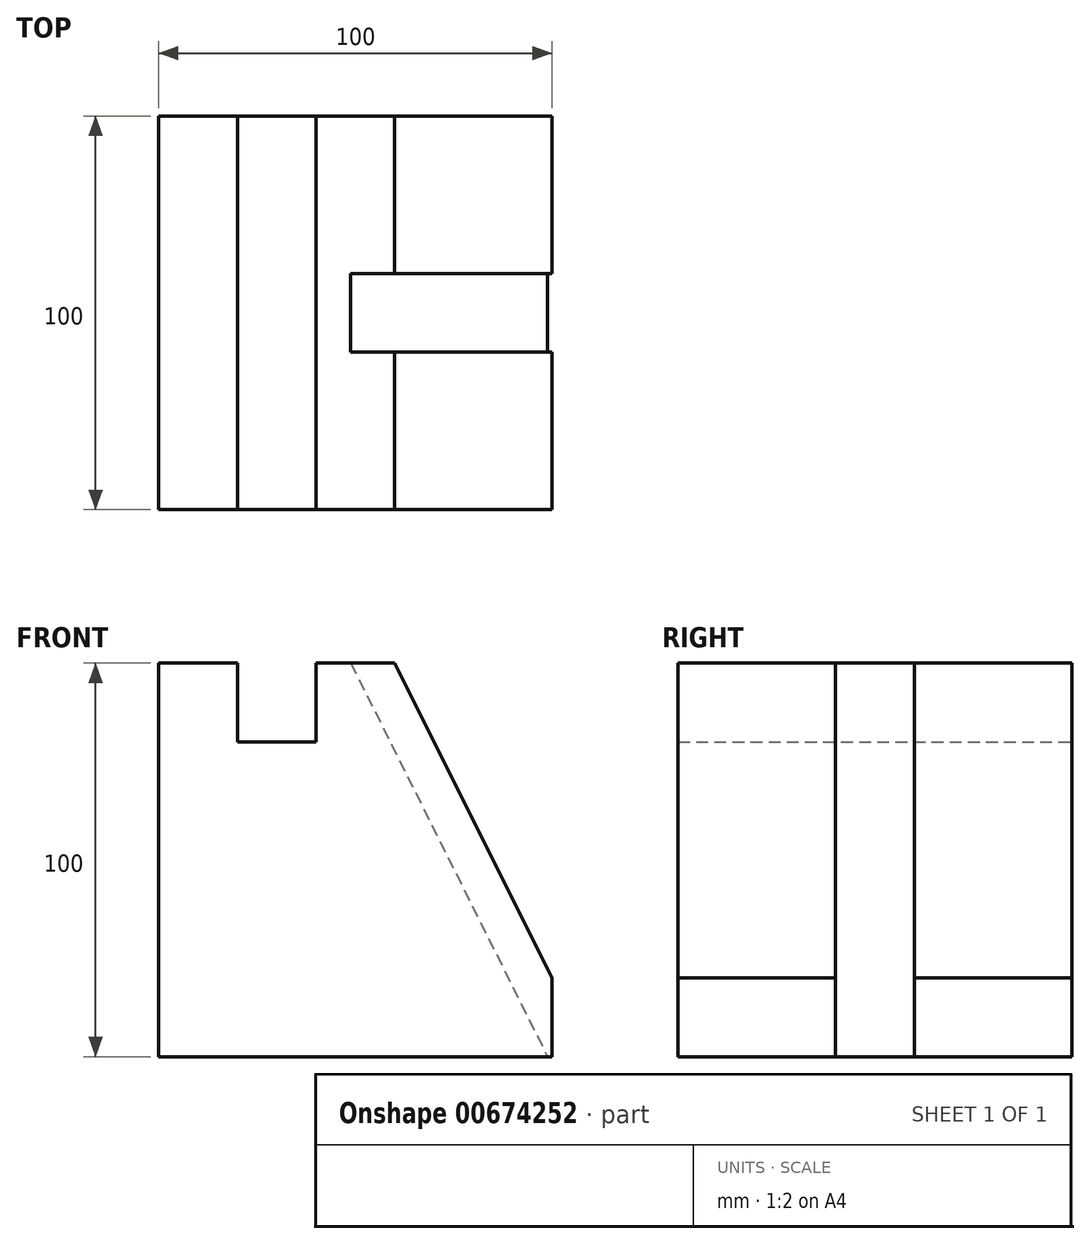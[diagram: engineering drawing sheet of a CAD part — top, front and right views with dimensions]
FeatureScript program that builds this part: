
annotation { "Feature Type Name" : "Feature", "Feature Type Description" : "" }
export const myFeature = defineFeature(function(context is Context, id is Id, definition is map)
    precondition{}
    {
        {
            var Q0;
            Q0=qCreatedBy(makeId("Front.planeOp"),FACE);
            var sketch = newSketch(context, id + "F0", { "sketchPlane" : qUnion([Q0])});
            skLineSegment(sketch, "E0", {"start": v(0, 0) * mm, "end": v(0, 100) * mm});
            skLineSegment(sketch, "E1", {"start": v(0, 0) * mm, "end": v(100, 0) * mm});
            skLineSegment(sketch, "E2", {"start": v(100, 0) * mm, "end": v(100, 20) * mm});
            skLineSegment(sketch, "E3", {"start": v(0, 100) * mm, "end": v(20, 100) * mm});
            skLineSegment(sketch, "E4", {"start": v(20, 100) * mm, "end": v(20, 80) * mm});
            skLineSegment(sketch, "E5", {"start": v(20, 80) * mm, "end": v(40, 80) * mm});
            skLineSegment(sketch, "E6", {"start": v(40, 80) * mm, "end": v(40, 100) * mm});
            skLineSegment(sketch, "E7", {"start": v(40, 100) * mm, "end": v(60, 100) * mm});
            skLineSegment(sketch, "E8", {"start": v(60, 100) * mm, "end": v(100, 20) * mm});
            skSolve(sketch);
        }
        {
            var Q0;
            Q0=makeQuery(id+"F0.imprint","IMPRINT",FACE,{"disambiguationData":[TD([[makeQuery(id+"F0.imprint","IMPRINT",EDGE,{"derivedFrom":sQuery(id+"F0.wireOp",EDGE,"E0")}),-1.0]])]});
            extrude(context, id + "F1", {"entities" : qUnion([Q0]), "depth" : 100 * mm, "offsetDistance" : 25 * mm});
        }
        {
            var Q0;
            Q0=makeQuery(id+"F1.opExtrude","SWEPT_FACE",FACE,{"disambiguationData":[OSD([sQuery(id+"F0.wireOp",EDGE,"E8")])]});
            var sketch = newSketch(context, id + "F2", { "sketchPlane" : qUnion([Q0])});
            skLineSegment(sketch, "E9", {"start": v(-100, 62.6) * mm, "end": v(-60, 62.6) * mm});
            skLineSegment(sketch, "E10", {"start": v(-60, 62.6) * mm, "end": v(-40, 62.6) * mm});
            skLineSegment(sketch, "E11", {"start": v(-40, 62.6) * mm, "end": v(0, 62.6) * mm});
            skLineSegment(sketch, "E12", {"start": v(-60, 62.6) * mm, "end": v(-60, -26.83) * mm});
            skLineSegment(sketch, "E13", {"start": v(-60, -26.83) * mm, "end": v(-40, -26.83) * mm});
            skLineSegment(sketch, "E14", {"start": v(-40, -26.83) * mm, "end": v(-40, 62.6) * mm});
            skSolve(sketch);
        }
        {
            var Q0;
            Q0=makeQuery(id+"F2.imprint","IMPRINT",FACE,{"disambiguationData":[TD([[makeQuery(id+"F2.imprint","IMPRINT",EDGE,{"derivedFrom":sQuery(id+"F2.wireOp",EDGE,"E12")}),1.0]])]});
            extrude(context, id + "F3", {"entities" : qUnion([Q0]), "operationType" : NewBodyOperationType.REMOVE, "oppositeDirection" : true, "depth" : 10 * mm, "offsetDistance" : 25 * mm});
        }
        {
            var Q0;
            Q0=makeQuery(id+"F3.boolean.opBoolean","COPY",FACE,{"derivedFrom":makeQuery(id+"F3.opExtrude","SWEPT_FACE",FACE,{"disambiguationData":[OSD([sQuery(id+"F2.wireOp",EDGE,"E10")])]})});
            extrude(context, id + "F4", {"entities" : qUnion([Q0]), "operationType" : NewBodyOperationType.REMOVE, "oppositeDirection" : true, "depth" : 10 * mm, "offsetDistance" : 25 * mm});
        }
        {
            var Q0;
            Q0=makeQuery(id+"F3.boolean.opBoolean","COPY",FACE,{"derivedFrom":makeQuery(id+"F3.opExtrude","SWEPT_FACE",FACE,{"disambiguationData":[OSD([sQuery(id+"F2.wireOp",EDGE,"E13")])]})});
            extrude(context, id + "F5", {"entities" : qUnion([Q0]), "operationType" : NewBodyOperationType.REMOVE, "oppositeDirection" : true, "depth" : 10 * mm, "offsetDistance" : 25 * mm});
        }
        {
            var Q0;
            Q0=makeQuery(id+"F5.boolean.opBoolean","COPY",FACE,{"derivedFrom":makeQuery(id+"F5.opExtrude","CAP_FACE",FACE,{"disambiguationData":[OSD([sQuery(id+"F2.wireOp",EDGE,"E13")])],"isStart":false})});
            extrude(context, id + "F6", {"entities" : qUnion([Q0]), "operationType" : NewBodyOperationType.REMOVE, "oppositeDirection" : true, "depth" : 10 * mm, "offsetDistance" : 25 * mm});
        }
    });
